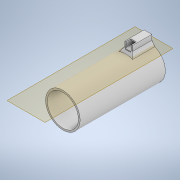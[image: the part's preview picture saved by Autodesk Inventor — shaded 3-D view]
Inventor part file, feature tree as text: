
AUTODESK INVENTOR PART (.ipt)
format: ipt  version: 2021 (Build 250183000, 183)  size: 798,208 bytes
history: native  units: in
note: dims shown in document units (in); Inventor stores cm internally (conversion verified against a paired STEP export)
features: projected_geometry x11, extrude x9, sketch x8, chamfer x5, plane x1, pattern_linear x1, fillet x1
ambient origin geometry x8: Origin, YZ Plane, XZ Plane, XY Plane, X Axis, Y Axis, Z Axis, Center Point
bodies: Solid1 (feature_tree)
feature tree (36):
  extrude  "Extrusion1"  Depth=4.3307in TaperAngle=0.0deg
  plane  "Work Plane1"
  extrude  "Extrusion7"  Depth=4.252in TaperAngle=0.0deg
  extrude  "Extrusion8"  Depth=0.3937in
  extrude  "Extrusion9"  Depth=0.3937in
  extrude  "Extrusion10"  Depth=0.1181in
  extrude  "Extrusion11"  Depth=0.0591in
  extrude  "Extrusion12"  Depth=0.0591in
  pattern_linear  "Rectangular Pattern3"  Spacing1=1.6929in  [1 undecoded]
  extrude  "Extrusion13"  Depth=0.0394in
  chamfer  "Chamfer2"  Distance=0.0394in
  chamfer  "Chamfer3"  Distance=0.0098in
  chamfer  "Chamfer4"  Distance=8.2677in
  chamfer  "Chamfer5"  Distance=0.248in
  extrude  "Extrusion14"  Depth=0.3937in TaperAngle=0.0deg
  chamfer  "Chamfer6"  Distance=0.0787in
  fillet  "Fillet10"  Radius=0.0059in
  sketch  "Sketch2"  dims[d2=1.752in d3=4.3307in d4=0.0in]
  sketch  "Sketch9"  dims[d54=1.5748in d55=4.252in d56=0.0in]
  projected_geometry  "Projected Loop7"
  sketch  "Sketch10"  dims[d57=0.3937in d58=0.9843in]
  projected_geometry  "Projected Loop8"
  sketch  "Sketch11"  dims[d59=0.3937in d60=0.0236in d61=0.0in d62=0.0in d63=0.1929in]
  projected_geometry  "Projected Loop9"
  sketch  "Sketch12"  dims[d64=0.122in d65=0.1181in]
  projected_geometry  "Projected Loop10"
  projected_geometry  "Projected Loop11"
  projected_geometry  "Projected Loop12"
  sketch  "Sketch14"  dims[d66=0.0551in d67=0.0in d68=0.0591in]
  projected_geometry  "Projected Loop14"
  projected_geometry  "Projected Loop15"
  sketch  "Sketch16"  dims[d69=0.0591in d70=0.0591in]
  projected_geometry  "Projected Loop16"
  sketch  "Sketch17"  dims[d71=0.935in d72=0.0in d76=1.6929in d77=0.0in d84=1.811in d85=0.0394in d86=0.0098in d87=0.0in d88=8.2677in d90=0.0787in d92=0.248in d93=0.3937in d94=0.0in d95=0.0787in d96=0.0059in d97=0.0157in d98=0.0787in d99=45.0deg d100=0.0118in d101=0.0787in d102=45.0deg d103=0.1575in d104=0.0787in d105=45.0deg d106=0.0098in d107=0.0787in d108=45.0deg d109=0.5906in d110=0.0433in d111=0.0in d112=0.0433in d113=0.0787in d114=45.0deg d115=0.0394in d19=0.0197in d20=0.0344in d21=0.0197in d22=0.0344in]
  projected_geometry  "Projected Loop17"
  projected_geometry  "Projected Loop18"
note: 1 required parameter value undecoded (feature->parameter linkage not recoverable at this tier; creation-order binding heuristic only, values carry confidence <= 0.55)
